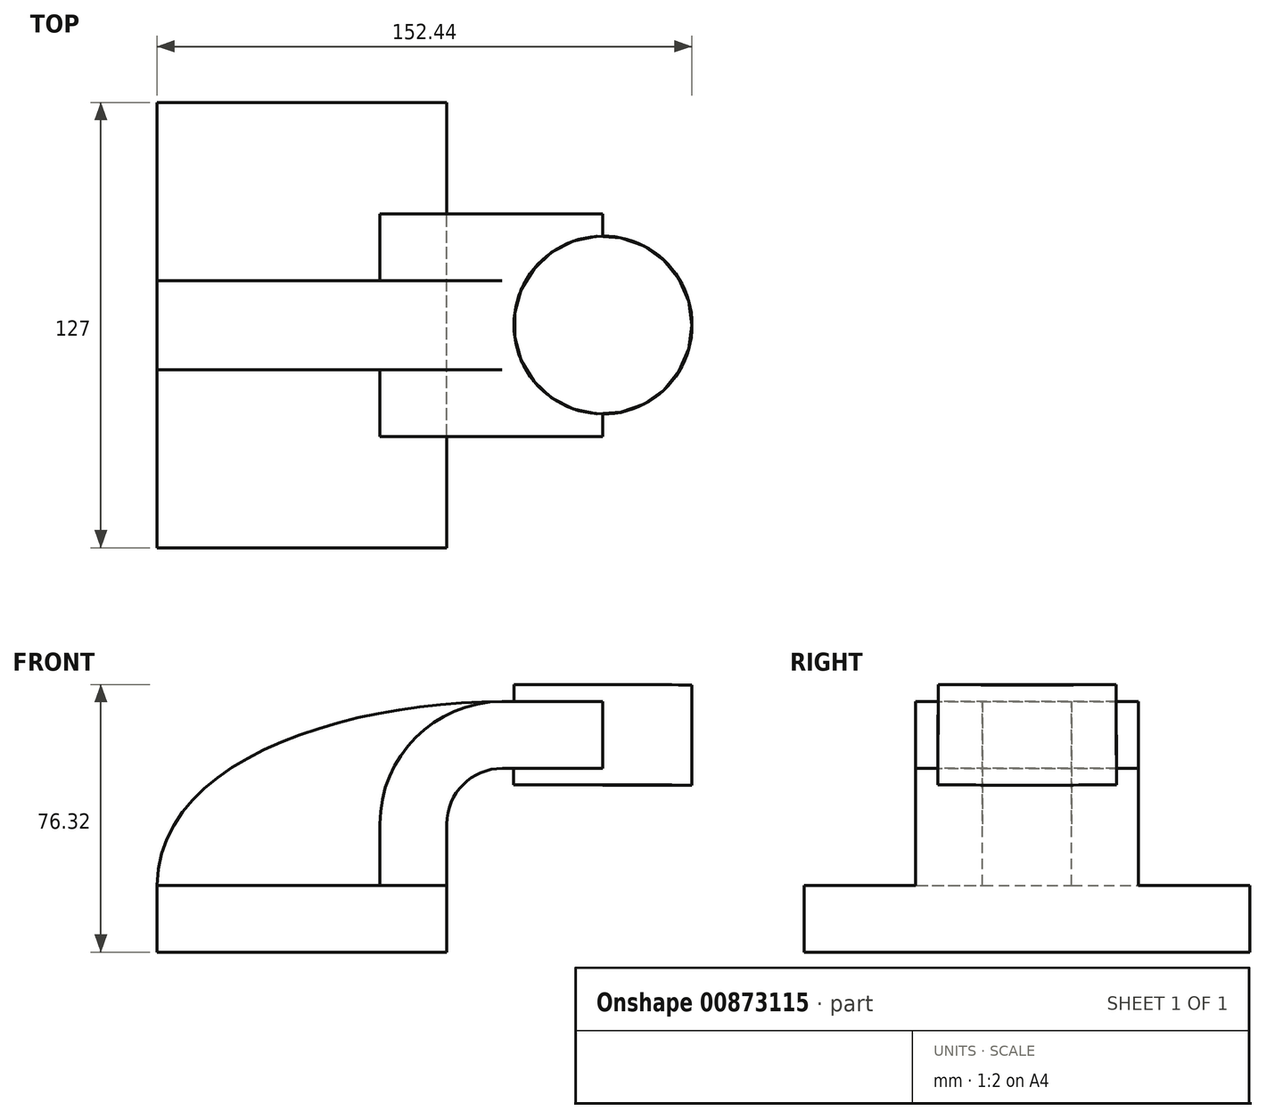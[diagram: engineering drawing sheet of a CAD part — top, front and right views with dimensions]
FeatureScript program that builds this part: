
annotation { "Feature Type Name" : "Feature", "Feature Type Description" : "" }
export const myFeature = defineFeature(function(context is Context, id is Id, definition is map)
    precondition{}
    {
        {
            var Q0;
            Q0=qCreatedBy(makeId("Front.planeOp"),FACE);
            var sketch = newSketch(context, id + "F0", { "sketchPlane" : qUnion([Q0])});
            skLineSegment(sketch, "E0.bottom", {"start": v(41.28, -9.52) * mm, "end": v(-41.28, -9.53) * mm});
            skLineSegment(sketch, "E0.top", {"start": v(41.28, 9.53) * mm, "end": v(-41.28, 9.53) * mm});
            skLineSegment(sketch, "E0.left", {"start": v(41.28, -9.52) * mm, "end": v(41.28, 9.53) * mm});
            skLineSegment(sketch, "E0.right", {"start": v(-41.28, -9.53) * mm, "end": v(-41.28, 9.53) * mm});
            skPoint(sketch, "E0.middle", {"position": v(0, 0) * mm});
            skLineSegment(sketch, "E1.bottom", {"start": v(111.16, 38.1) * mm, "end": v(60.36, 38.1) * mm});
            skLineSegment(sketch, "E1.top", {"start": v(111.16, 66.68) * mm, "end": v(60.36, 66.68) * mm});
            skLineSegment(sketch, "E1.left", {"start": v(111.16, 38.1) * mm, "end": v(111.16, 66.67) * mm});
            skLineSegment(sketch, "E1.right", {"start": v(60.36, 38.1) * mm, "end": v(60.36, 66.67) * mm});
            skPoint(sketch, "E1.middle", {"position": v(85.76, 52.39) * mm});
            skLineSegment(sketch, "E2", {"start": v(41.28, 9.53) * mm, "end": v(41.28, 27) * mm});
            skArc(sketch, "E3", {"start": v(57.15, 42.88) * mm, "mid": v(45.92, 38.23) * mm, "end": v(41.27, 27) * mm});
            skLineSegment(sketch, "E4", {"start": v(57.15, 42.88) * mm, "end": v(85.72, 42.88) * mm});
            skLineSegment(sketch, "E5.0", {"start": v(57.15, 61.93) * mm, "end": v(85.72, 61.93) * mm});
            skArc(sketch, "E5.1", {"start": v(57.15, 61.93) * mm, "mid": v(32.45, 51.7) * mm, "end": v(22.23, 27) * mm});
            skLineSegment(sketch, "E5.2", {"start": v(22.22, 9.53) * mm, "end": v(22.22, 27) * mm});
            skFitSpline(sketch, "E6", {"points": [v(-41.28, 9.52) * mm, v(57.15, 61.93) * mm], "startDerivative": vector(1.11, 109.05) * mm, "endDerivative": vector(131.01, 0.23) * mm});
            skLineSegment(sketch, "E7", {"start": v(85.79, 66.68) * mm, "end": v(85.72, 38.1) * mm});
            skLineSegment(sketch, "E8", {"start": v(85.72, 61.93) * mm, "end": v(85.72, 42.88) * mm});
            skSolve(sketch);
        }
        {
            var Q0;
            Q0=makeQuery(id+"F0.imprint","IMPRINT",FACE,{"disambiguationData":[TD([[makeQuery(id+"F0.imprint","IMPRINT",EDGE,{"derivedFrom":sQuery(id+"F0.wireOp",EDGE,"E0.bottom")}),-1.0]])]});
            extrude(context, id + "F1", {"entities" : qUnion([Q0]), "endBound" : BoundingType.SYMMETRIC, "depth" : 127 * mm, "offsetDistance" : 25.4 * mm});
        }
        {
            var Q0;
            {var subQ1=sQuery(id+"F0.wireOp",EDGE,"E2");Q0=makeQuery(id+"F0.imprint","IMPRINT",FACE,{"disambiguationData":[TD([[makeQuery(id+"F0.imprint","IMPRINT",EDGE,{"derivedFrom":subQ1}),1.0]])]});}
            var Q1;
            {var subQ5=sQuery(id+"F0.wireOp",EDGE,"E8");Q1=makeQuery(id+"F0.imprint","IMPRINT",FACE,{"disambiguationData":[TD([[makeQuery(id+"F0.imprint","IMPRINT",EDGE,{"derivedFrom":subQ5}),-1.0]])]});}
            extrude(context, id + "F2", {"entities" : qUnion([Q0, Q1]), "operationType" : NewBodyOperationType.ADD, "endBound" : BoundingType.SYMMETRIC, "depth" : 63.5 * mm, "offsetDistance" : 25.4 * mm});
        }
        {
            var Q0;
            {var subQ4=sQuery(id+"F0.wireOp",EDGE,"E5.1");Q0=makeQuery(id+"F0.imprint","IMPRINT",FACE,{"disambiguationData":[TD([[makeQuery(id+"F0.imprint","IMPRINT",EDGE,{"derivedFrom":subQ4}),-1.0]])]});}
            extrude(context, id + "F3", {"entities" : qUnion([Q0]), "operationType" : NewBodyOperationType.ADD, "endBound" : BoundingType.SYMMETRIC, "depth" : 25.4 * mm, "offsetDistance" : 25.4 * mm});
        }
        {
            var Q0;
            {var subQ0=sQuery(id+"F0.wireOp",EDGE,"E1.left");Q0=makeQuery(id+"F0.imprint","IMPRINT",FACE,{"disambiguationData":[TD([[makeQuery(id+"F0.imprint","IMPRINT",EDGE,{"derivedFrom":subQ0}),1.0]])]});}
            var Q1;
            Q1=sQuery(id+"F0.wireOp",EDGE,"E7");
            revolve(context, id + "F4", {"operationType" : NewBodyOperationType.ADD, "surfaceOperationType" : NewSurfaceOperationType.NEW, "entities" : qUnion([Q0]), "axis" : qUnion([Q1]), "revolveType" : RevolveType.FULL});
        }
    });
